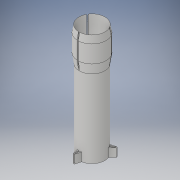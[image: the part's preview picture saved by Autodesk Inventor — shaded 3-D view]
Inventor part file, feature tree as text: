
AUTODESK INVENTOR PART (.ipt)
format: ipt  version: 2017 (Build 210142000, 142)  size: 190,464 bytes
history: native  units: in
note: dims shown in document units (in); Inventor stores cm internally (conversion verified against a paired STEP export)
features: extrude x3, sketch x2, plane x1, revolve x1
ambient origin geometry x8: Origin, YZ Plane, XZ Plane, XY Plane, X Axis, Y Axis, Z Axis, Center Point
bodies: Solid1 (feature_tree)
feature tree (7):
  sketch  "Sketch1"  dims[d0=0.475in d1=3.6in]
  plane  "Work Plane1"
  sketch  "Sketch2"  dims[d10=0.025in d11=0.025in d12=0.025in d13=0.025in d14=0.025in d15=0.025in d24=0.24in d25=0.24in d27=0.24in d28=0.24in d29=0.24in d30=0.35in d31=0.0in d32=4.9125in d33=0.0in d39=0.535in d41=180.0deg d43=90.0deg d44=6.875in d45=0.0in]
  extrude  "Extrusion1"  Depth=3.6in
  extrude  "Extrusion2"  Depth=0.025in
  revolve  "Revolution2"  [1 undecoded]
  extrude  "Extrusion3"  Depth=0.025in
note: 1 required parameter value undecoded (feature->parameter linkage not recoverable at this tier; creation-order binding heuristic only, values carry confidence <= 0.55)
